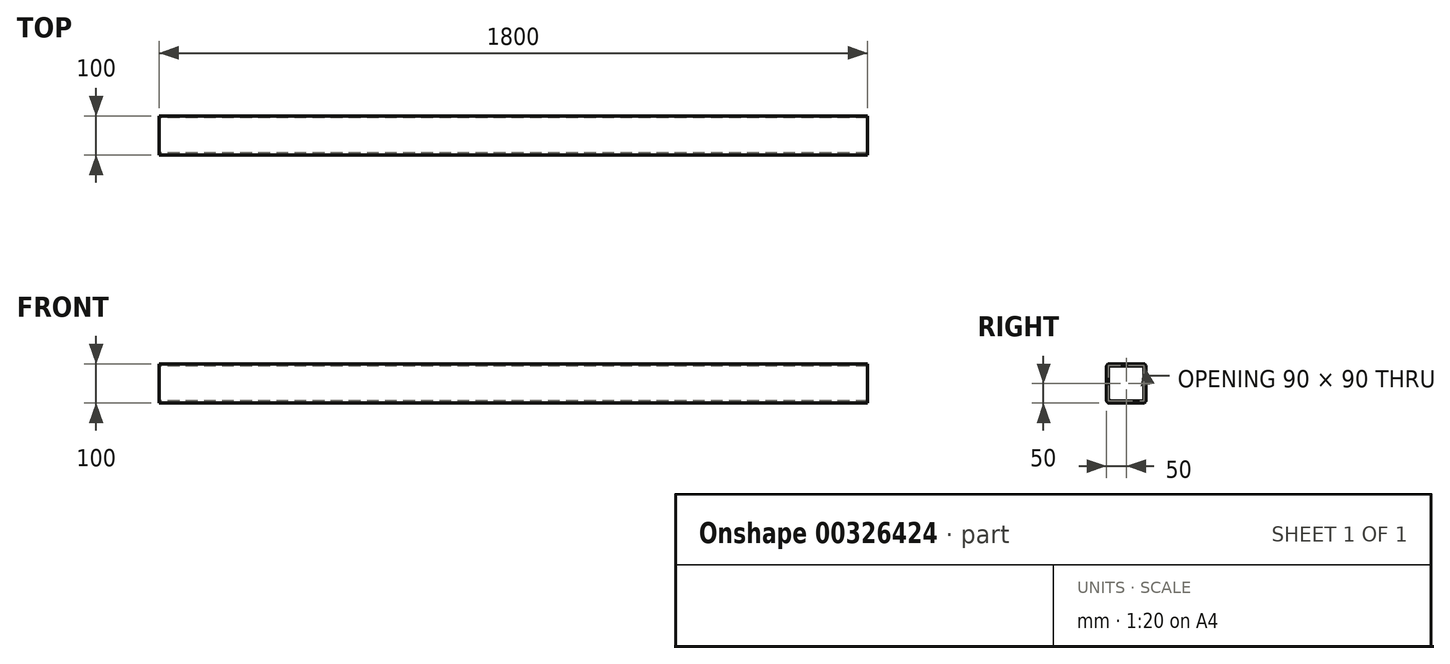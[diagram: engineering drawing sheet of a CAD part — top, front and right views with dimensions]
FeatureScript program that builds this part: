
annotation { "Feature Type Name" : "Feature", "Feature Type Description" : "" }
export const myFeature = defineFeature(function(context is Context, id is Id, definition is map)
    precondition{}
    {
        {
            var Q0;
            Q0=qCreatedBy(makeId("Front.planeOp"),FACE);
            var sketch = newSketch(context, id + "F0", { "sketchPlane" : qUnion([Q0])});
            skLineSegment(sketch, "E0.bottom", {"start": v(900, -50) * mm, "end": v(-900, -50) * mm});
            skLineSegment(sketch, "E0.top", {"start": v(900, 50) * mm, "end": v(-900, 50) * mm});
            skLineSegment(sketch, "E0.left", {"start": v(900, -50) * mm, "end": v(900, 50) * mm});
            skLineSegment(sketch, "E0.right", {"start": v(-900, -50) * mm, "end": v(-900, 50) * mm});
            skPoint(sketch, "E0.middle", {"position": v(0, 0) * mm});
            skSolve(sketch);
        }
        {
            var Q0;
            Q0=makeQuery(id+"F0.imprint","IMPRINT",FACE,{"disambiguationData":[TD([[makeQuery(id+"F0.imprint","IMPRINT",EDGE,{"derivedFrom":sQuery(id+"F0.wireOp",EDGE,"E0.bottom")}),-1.0]])]});
            extrude(context, id + "F1", {"entities" : qUnion([Q0]), "depth" : 100 * mm, "offsetDistance" : 25 * mm});
        }
        {
            var Q0;
            Q0=makeQuery(id+"F1.opExtrude","SWEPT_FACE",FACE,{"disambiguationData":[OSD([sQuery(id+"F0.wireOp",EDGE,"E0.right")])]});
            var Q1;
            Q1=makeQuery(id+"F1.opExtrude","SWEPT_FACE",FACE,{"disambiguationData":[OSD([sQuery(id+"F0.wireOp",EDGE,"E0.left")])]});
            shell(context, id + "F2", {"entities" : qUnion([Q0, Q1]), "thickness" : 5 * mm});
        }
        {
            var Q0;
            Q0=makeQuery(id+"F1.opExtrude","CAP_EDGE",EDGE,{"disambiguationData":[OSD([sQuery(id+"F0.wireOp",EDGE,"E0.top")])],"isStart":false});
            var Q1;
            Q1=makeQuery(id+"F1.opExtrude","CAP_EDGE",EDGE,{"disambiguationData":[OSD([sQuery(id+"F0.wireOp",EDGE,"E0.top")])],"isStart":true});
            var Q2;
            Q2=makeQuery(id+"F1.opExtrude","CAP_EDGE",EDGE,{"disambiguationData":[OSD([sQuery(id+"F0.wireOp",EDGE,"E0.bottom")])],"isStart":false});
            var Q3;
            Q3=makeQuery(id+"F1.opExtrude","CAP_EDGE",EDGE,{"disambiguationData":[OSD([sQuery(id+"F0.wireOp",EDGE,"E0.bottom")])],"isStart":true});
            var Q4;
            {var subQ0=sQuery(id+"F0.wireOp",EDGE,"E0.top");Q4=makeQuery(id+"F2.opShell","OFFSET_EDGE",EDGE,{"disambiguationData":[OSD([subQ0]),TDD([makeQuery(id+"F1.opExtrude","CAP_EDGE",EDGE,{"disambiguationData":[OSD([subQ0])],"isStart":true})])]});}
            var Q5;
            {var subQ0=sQuery(id+"F0.wireOp",EDGE,"E0.top");Q5=makeQuery(id+"F2.opShell","OFFSET_EDGE",EDGE,{"disambiguationData":[OSD([subQ0]),TDD([makeQuery(id+"F1.opExtrude","CAP_EDGE",EDGE,{"disambiguationData":[OSD([subQ0])],"isStart":false})])]});}
            var Q6;
            {var subQ0=sQuery(id+"F0.wireOp",EDGE,"E0.bottom");Q6=makeQuery(id+"F2.opShell","OFFSET_EDGE",EDGE,{"disambiguationData":[OSD([subQ0]),TDD([makeQuery(id+"F1.opExtrude","CAP_EDGE",EDGE,{"disambiguationData":[OSD([subQ0])],"isStart":true})])]});}
            var Q7;
            {var subQ0=sQuery(id+"F0.wireOp",EDGE,"E0.bottom");Q7=makeQuery(id+"F2.opShell","OFFSET_EDGE",EDGE,{"disambiguationData":[OSD([subQ0]),TDD([makeQuery(id+"F1.opExtrude","CAP_EDGE",EDGE,{"disambiguationData":[OSD([subQ0])],"isStart":false})])]});}
            fillet(context, id + "F3", {"entities" : qUnion([Q0, Q1, Q2, Q3, Q4, Q5, Q6, Q7]), "radius" : 7 * mm, "tangentPropagation" : true, "allowEdgeOverflow" : false});
        }
    });
